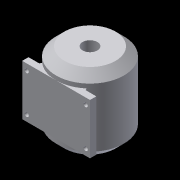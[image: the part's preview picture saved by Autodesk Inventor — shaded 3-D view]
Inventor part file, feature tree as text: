
AUTODESK INVENTOR PART (.ipt)
format: ipt  version: 2020 (Build 240168000, 168)  size: 126,464 bytes
history: native  units: mm
features: extrude x4, other x1, chamfer x1
ambient origin geometry x8: Origin, YZ Plane, XZ Plane, XY Plane, X Axis, Y Axis, Z Axis, Center Point
bodies: Body1 (feature_tree)
feature tree (6):
  other  "實體1"
  extrude  "Extrusion1"  Depth=16.1mm
  extrude  "Extrusion2"  TaperAngle=30.0deg  [1 undecoded]
  chamfer  "Chamfer1"  Distance=1.5mm
  extrude  "Extrusion3"  Depth=1.5mm
  extrude  "Extrusion4"  Depth=12.0mm TaperAngle=0.0deg
note: 1 required parameter value undecoded (feature->parameter linkage not recoverable at this tier; creation-order binding heuristic only, values carry confidence <= 0.55)
